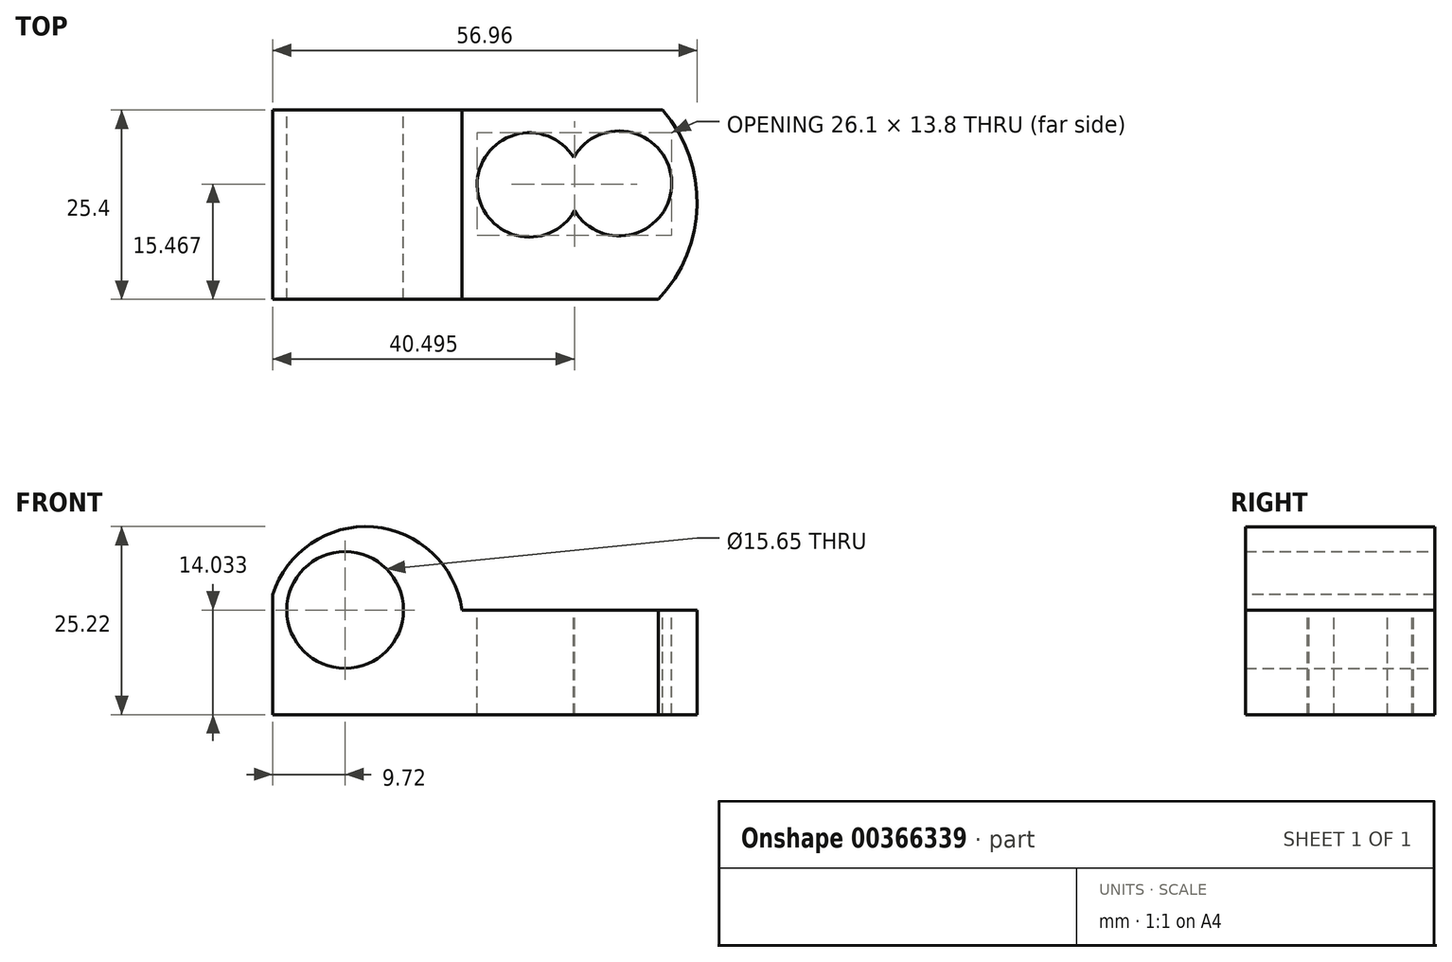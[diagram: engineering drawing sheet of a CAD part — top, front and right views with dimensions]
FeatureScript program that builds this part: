
annotation { "Feature Type Name" : "Feature", "Feature Type Description" : "" }
export const myFeature = defineFeature(function(context is Context, id is Id, definition is map)
    precondition{}
    {
        {
            var Q0;
            Q0=qCreatedBy(makeId("Front.planeOp"),FACE);
            var sketch = newSketch(context, id + "F0", { "sketchPlane" : qUnion([Q0])});
            skLineSegment(sketch, "E0", {"start": v(-25.4, 25.4) * mm, "end": v(-25.4, 0) * mm});
            skLineSegment(sketch, "E1", {"start": v(-25.4, 25.4) * mm, "end": v(0, 25.4) * mm});
            skLineSegment(sketch, "E2", {"start": v(0, 25.4) * mm, "end": v(0, 14.03) * mm});
            skLineSegment(sketch, "E3", {"start": v(0, 14.03) * mm, "end": v(31.75, 14.03) * mm});
            skLineSegment(sketch, "E4", {"start": v(31.75, 14.03) * mm, "end": v(31.75, 0) * mm});
            skLineSegment(sketch, "E5", {"start": v(31.75, 0) * mm, "end": v(-25.4, 0) * mm});
            skCircle(sketch, "E6", {"center": v(-15.68, 14.03) * mm, "radius": 7.83 * mm});
            skSolve(sketch);
        }
        {
            var Q0;
            Q0=makeQuery(id+"F0.imprint","IMPRINT",FACE,{"disambiguationData":[TD([[makeQuery(id+"F0.imprint","IMPRINT",EDGE,{"derivedFrom":sQuery(id+"F0.wireOp",EDGE,"E0")}),1.0]])]});
            extrude(context, id + "F1", {"entities" : qUnion([Q0]), "depth" : 25.4 * mm});
        }
        {
            var Q0;
            Q0=makeQuery(id+"F1.opExtrude","SWEPT_FACE",FACE,{"disambiguationData":[OSD([sQuery(id+"F0.wireOp",EDGE,"E3")])]});
            var sketch = newSketch(context, id + "F2", { "sketchPlane" : qUnion([Q0])});
            skCircle(sketch, "E7", {"center": v(9.05, -10.05) * mm, "radius": 7 * mm});
            skCircle(sketch, "E8", {"center": v(21.1, -9.85) * mm, "radius": 7.04 * mm});
            skSolve(sketch);
        }
        {
            var Q0;
            Q0 = qSketchRegion(id + "F2", true);
            extrude(context, id + "F3", {"entities" : qUnion([Q0]), "operationType" : NewBodyOperationType.REMOVE, "oppositeDirection" : true, "depth" : 25.4 * mm});
        }
        {
            var Q0;
            Q0=makeQuery(id+"F1.opExtrude","SWEPT_FACE",FACE,{"disambiguationData":[OSD([sQuery(id+"F0.wireOp",EDGE,"E3")])]});
            var sketch = newSketch(context, id + "F4", { "sketchPlane" : qUnion([Q0])});
            skArc(sketch, "E9", {"start": v(26.33, -25.4) * mm, "mid": v(31.55, -12.82) * mm, "end": v(26.94, 0) * mm});
            skSolve(sketch);
        }
        {
            var Q0;
            {var subQ0=sQuery(id+"F4.wireOp",EDGE,"E9");Q0=makeQuery(id+"F4.imprint","IMPRINT",FACE,{"disambiguationData":[TD([[makeQuery(id+"F4.imprint","IMPRINT",EDGE,{"derivedFrom":subQ0}),-1.0]])]});}
            extrude(context, id + "F5", {"entities" : qUnion([Q0]), "operationType" : NewBodyOperationType.REMOVE, "oppositeDirection" : true, "depth" : 25.4 * mm});
        }
        {
            var Q0;
            Q0=makeQuery(id+"F1.opExtrude","CAP_FACE",FACE,{"disambiguationData":[OSD([sQuery(id+"F0.wireOp",EDGE,"E0"),sQuery(id+"F0.wireOp",EDGE,"E1"),sQuery(id+"F0.wireOp",EDGE,"E2"),sQuery(id+"F0.wireOp",EDGE,"E3"),sQuery(id+"F0.wireOp",EDGE,"E4"),sQuery(id+"F0.wireOp",EDGE,"E5"),sQuery(id+"F0.wireOp",EDGE,"E6")])],"isStart":false});
            var sketch = newSketch(context, id + "F6", { "sketchPlane" : qUnion([Q0])});
            skArc(sketch, "E10", {"start": v(0, 14.03) * mm, "mid": v(-11.88, 25.18) * mm, "end": v(-25.4, 16.08) * mm});
            skSolve(sketch);
        }
        {
            var Q0;
            {var subQ0=sQuery(id+"F6.wireOp",EDGE,"E10");Q0=makeQuery(id+"F6.imprint","IMPRINT",FACE,{"disambiguationData":[TD([[makeQuery(id+"F6.imprint","IMPRINT",EDGE,{"derivedFrom":subQ0}),-1.0]])]});}
            extrude(context, id + "F7", {"entities" : qUnion([Q0]), "operationType" : NewBodyOperationType.REMOVE, "oppositeDirection" : true, "depth" : 25.4 * mm});
        }
    });
